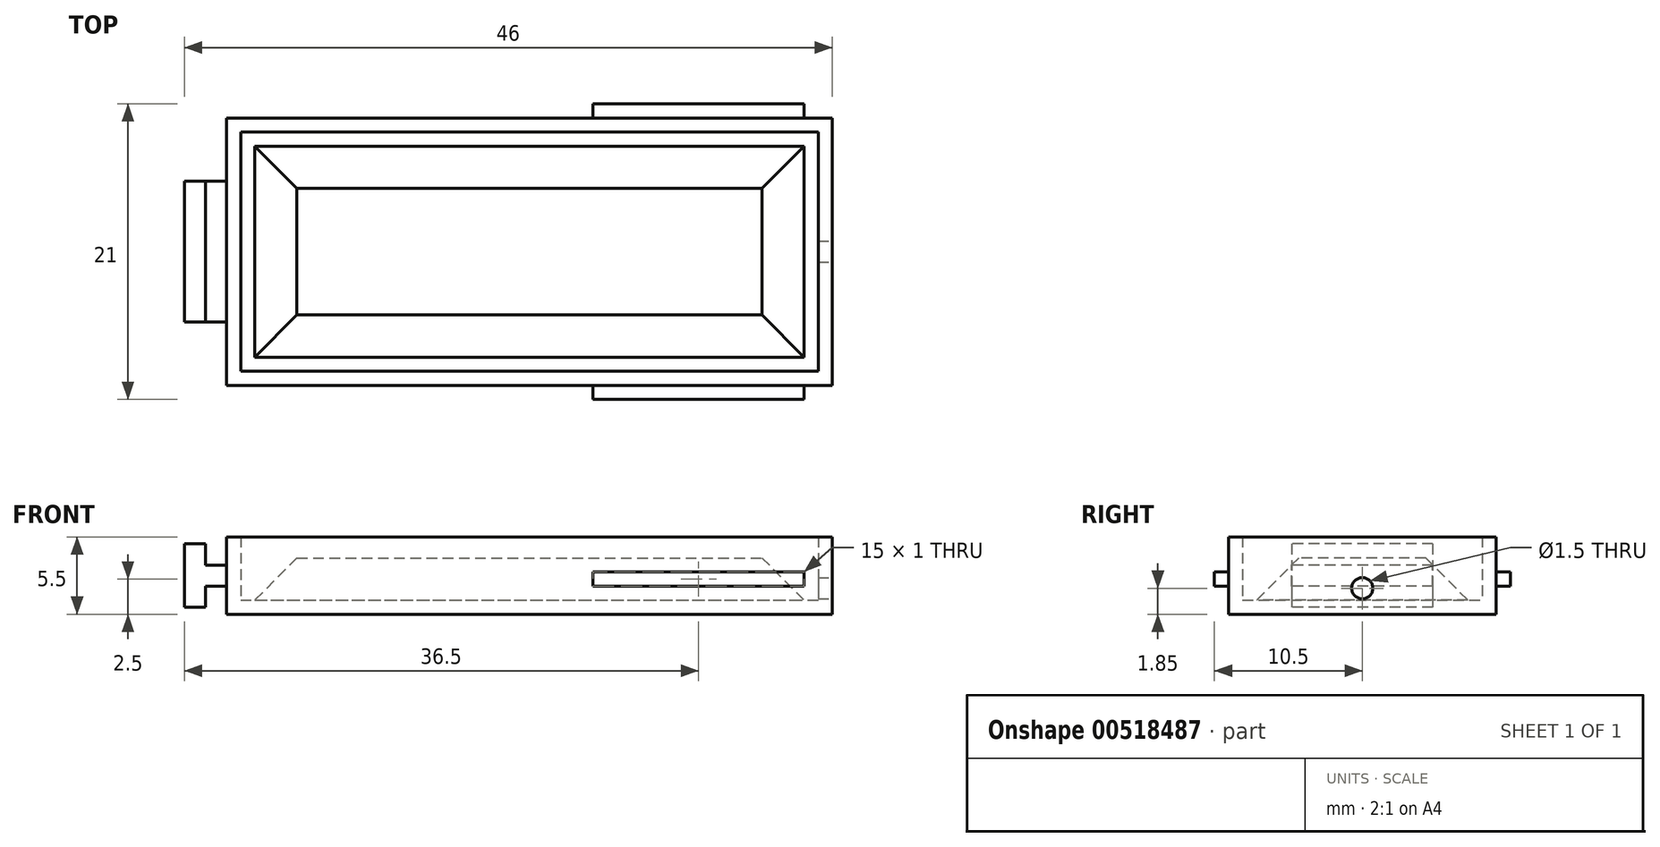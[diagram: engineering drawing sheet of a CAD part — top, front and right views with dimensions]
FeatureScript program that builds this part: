
annotation { "Feature Type Name" : "Feature", "Feature Type Description" : "" }
export const myFeature = defineFeature(function(context is Context, id is Id, definition is map)
    precondition{}
    {
        {
            var Q0;
            Q0=qCreatedBy(makeId("Top.planeOp"),FACE);
            var sketch = newSketch(context, id + "F0", { "sketchPlane" : qUnion([Q0])});
            skLineSegment(sketch, "E0.bottom", {"start": v(0, 9) * mm, "end": v(33, 9) * mm, "construction": true});
            skLineSegment(sketch, "E0.top", {"start": v(0, 0) * mm, "end": v(33, 0) * mm, "construction": true});
            skLineSegment(sketch, "E0.left", {"start": v(0, 9) * mm, "end": v(0, 0) * mm, "construction": true});
            skLineSegment(sketch, "E0.right", {"start": v(33, 9) * mm, "end": v(33, 0) * mm, "construction": true});
            skLineSegment(sketch, "E1.bottom", {"start": v(-3, 12) * mm, "end": v(36, 12) * mm});
            skLineSegment(sketch, "E1.top", {"start": v(-3, -3) * mm, "end": v(36, -3) * mm});
            skLineSegment(sketch, "E1.left", {"start": v(-3, 12) * mm, "end": v(-3, -3) * mm});
            skLineSegment(sketch, "E1.right", {"start": v(36, 12) * mm, "end": v(36, -3) * mm});
            skLineSegment(sketch, "E2", {"start": v(16.5, -23.39) * mm, "end": v(16.5, 35.98) * mm, "construction": true});
            skPoint(sketch, "E2.startSnap0", {"position": v(16.5, 12) * mm});
            skPoint(sketch, "E2.endSnap0", {"position": v(16.5, 12) * mm});
            skPoint(sketch, "E3", {"position": v(16.5, 0) * mm});
            skLineSegment(sketch, "E4", {"start": v(-3, 4.5) * mm, "end": v(36, 4.5) * mm, "construction": true});
            skPoint(sketch, "E4.startSnap0", {"position": v(0, 4.5) * mm});
            skPoint(sketch, "E4.startSnap1", {"position": v(-3, 4.5) * mm});
            skSolve(sketch);
        }
        {
            var Q0;
            Q0=qCreatedBy(makeId("Top.planeOp"),FACE);
            cPlane(context, id + "F1", {"entities" : qUnion([Q0]), "cplaneType" : CPlaneType.OFFSET, "offset" : 3 * mm, "width" : 150 * mm, "height" : 150 * mm});
        }
        {
            var Q0;
            Q0=qCreatedBy(id+"F1.planeOp",FACE);
            var sketch = newSketch(context, id + "F2", { "sketchPlane" : qUnion([Q0])});
            skLineSegment(sketch, "E5.0", {"start": v(0, 9) * mm, "end": v(33, 9) * mm});
            skLineSegment(sketch, "E5.1", {"start": v(0, 9) * mm, "end": v(0, 0) * mm});
            skLineSegment(sketch, "E5.2", {"start": v(0, 0) * mm, "end": v(33, 0) * mm});
            skLineSegment(sketch, "E5.3", {"start": v(33, 9) * mm, "end": v(33, 0) * mm});
            skLineSegment(sketch, "E6", {"start": v(0, 4.5) * mm, "end": v(33, 4.5) * mm, "construction": true});
            skSolve(sketch);
        }
        {
            var Q0;
            Q0=makeQuery(id+"F2.imprint","IMPRINT",FACE,{"disambiguationData":[TD([[makeQuery(id+"F2.imprint","IMPRINT",EDGE,{"derivedFrom":sQuery(id+"F2.wireOp",EDGE,"E5.0")}),-1.0]])]});
            var Q1;
            Q1=makeQuery(id+"F0.imprint","IMPRINT",FACE,{"disambiguationData":[TD([[makeQuery(id+"F0.imprint","IMPRINT",EDGE,{"derivedFrom":sQuery(id+"F0.wireOp",EDGE,"E1.bottom")}),-1.0]])]});
            loft(context, id + "F3", {"sheetProfilesArray" : [{ "sheetProfileEntities" : qUnion([Q0]) }, { "sheetProfileEntities" : qUnion([Q1]) }]});
        }
        {
            var Q0;
            Q0=qCreatedBy(id+"F1.planeOp",FACE);
            var sketch = newSketch(context, id + "F4", { "sketchPlane" : qUnion([Q0])});
            skLineSegment(sketch, "E7.0", {"start": v(0, 9) * mm, "end": v(33, 9) * mm, "construction": true});
            skLineSegment(sketch, "E7.1", {"start": v(0, 9) * mm, "end": v(0, 0) * mm, "construction": true});
            skLineSegment(sketch, "E7.2", {"start": v(0, 0) * mm, "end": v(33, 0) * mm, "construction": true});
            skLineSegment(sketch, "E7.3", {"start": v(33, 9) * mm, "end": v(33, 0) * mm, "construction": true});
            skLineSegment(sketch, "E8.bottom", {"start": v(25, 8) * mm, "end": v(32, 8) * mm});
            skLineSegment(sketch, "E8.top", {"start": v(25, 1) * mm, "end": v(32, 1) * mm});
            skLineSegment(sketch, "E8.left", {"start": v(25, 8) * mm, "end": v(25, 1) * mm});
            skLineSegment(sketch, "E8.right", {"start": v(32, 8) * mm, "end": v(32, 1) * mm});
            skLineSegment(sketch, "E9.1.0.0", {"start": v(17, 8) * mm, "end": v(24, 8) * mm});
            skLineSegment(sketch, "E9.1.0.1", {"start": v(17, 8) * mm, "end": v(17, 1) * mm});
            skLineSegment(sketch, "E9.1.0.2", {"start": v(17, 1) * mm, "end": v(24, 1) * mm});
            skLineSegment(sketch, "E9.1.0.3", {"start": v(24, 8) * mm, "end": v(24, 1) * mm});
            skLineSegment(sketch, "E9.2.0.0", {"start": v(9, 8) * mm, "end": v(16, 8) * mm});
            skLineSegment(sketch, "E9.2.0.1", {"start": v(9, 8) * mm, "end": v(9, 1) * mm});
            skLineSegment(sketch, "E9.2.0.2", {"start": v(9, 1) * mm, "end": v(16, 1) * mm});
            skLineSegment(sketch, "E9.2.0.3", {"start": v(16, 8) * mm, "end": v(16, 1) * mm});
            skLineSegment(sketch, "E9.3.0.0", {"start": v(1, 8) * mm, "end": v(8, 8) * mm});
            skLineSegment(sketch, "E9.3.0.1", {"start": v(1, 8) * mm, "end": v(1, 1) * mm});
            skLineSegment(sketch, "E9.3.0.2", {"start": v(1, 1) * mm, "end": v(8, 1) * mm});
            skLineSegment(sketch, "E9.3.0.3", {"start": v(8, 8) * mm, "end": v(8, 1) * mm});
            skLineSegment(sketch, "E9.direction1", {"start": v(25, 8) * mm, "end": v(17, 8) * mm, "construction": true});
            skSolve(sketch);
        }
        {
            var Q0;
            Q0=makeQuery(id+"F4.imprint","IMPRINT",FACE,{"disambiguationData":[TD([[makeQuery(id+"F4.imprint","IMPRINT",EDGE,{"derivedFrom":sQuery(id+"F4.wireOp",EDGE,"E8.bottom")}),-1.0]])]});
            var Q1;
            Q1=makeQuery(id+"F4.imprint","IMPRINT",FACE,{"disambiguationData":[TD([[makeQuery(id+"F4.imprint","IMPRINT",EDGE,{"derivedFrom":sQuery(id+"F4.wireOp",EDGE,"E9.1.0.0")}),-1.0]])]});
            var Q2;
            Q2=makeQuery(id+"F4.imprint","IMPRINT",FACE,{"disambiguationData":[TD([[makeQuery(id+"F4.imprint","IMPRINT",EDGE,{"derivedFrom":sQuery(id+"F4.wireOp",EDGE,"E9.2.0.0")}),-1.0]])]});
            var Q3;
            Q3=makeQuery(id+"F4.imprint","IMPRINT",FACE,{"disambiguationData":[TD([[makeQuery(id+"F4.imprint","IMPRINT",EDGE,{"derivedFrom":sQuery(id+"F4.wireOp",EDGE,"E9.3.0.0")}),-1.0]])]});
            extrude(context, id + "F5", {"entities" : qUnion([Q0, Q1, Q2, Q3]), "operationType" : NewBodyOperationType.REMOVE, "oppositeDirection" : true, "depth" : .5 * mm, "offsetDistance" : 25 * mm});
        }
        {
            var Q0;
            Q0=makeQuery(id+"F4.imprint","IMPRINT",FACE,{"disambiguationData":[TD([[makeQuery(id+"F4.imprint","IMPRINT",EDGE,{"derivedFrom":sQuery(id+"F4.wireOp",EDGE,"E9.3.0.0")}),-1.0]])]});
            var Q1;
            Q1=makeQuery(id+"F4.imprint","IMPRINT",FACE,{"disambiguationData":[TD([[makeQuery(id+"F4.imprint","IMPRINT",EDGE,{"derivedFrom":sQuery(id+"F4.wireOp",EDGE,"E9.2.0.0")}),-1.0]])]});
            var Q2;
            Q2=makeQuery(id+"F4.imprint","IMPRINT",FACE,{"disambiguationData":[TD([[makeQuery(id+"F4.imprint","IMPRINT",EDGE,{"derivedFrom":sQuery(id+"F4.wireOp",EDGE,"E9.1.0.0")}),-1.0]])]});
            var Q3;
            Q3=makeQuery(id+"F4.imprint","IMPRINT",FACE,{"disambiguationData":[TD([[makeQuery(id+"F4.imprint","IMPRINT",EDGE,{"derivedFrom":sQuery(id+"F4.wireOp",EDGE,"E8.bottom")}),-1.0]])]});
            extrude(context, id + "F6", {"entities" : qUnion([Q0, Q1, Q2, Q3]), "oppositeDirection" : true, "depth" : .5 * mm, "offsetDistance" : 25 * mm});
        }
        {
            var Q0;
            Q0=makeQuery(id+"F3.opLoft","CAP_FACE",FACE,{"disambiguationData":[OSD([makeQuery(id+"F0.imprint","IMPRINT",FACE,{"disambiguationData":[TD([[makeQuery(id+"F0.imprint","IMPRINT",EDGE,{"derivedFrom":sQuery(id+"F0.wireOp",EDGE,"E1.bottom")}),-1.0]])]})])],"isStart":true});
            var sketch = newSketch(context, id + "F7", { "sketchPlane" : qUnion([Q0])});
            skLineSegment(sketch, "E10", {"start": v(50.67, -4.5) * mm, "end": v(-14.18, -4.5) * mm, "construction": true});
            skPoint(sketch, "E10.startSnap0", {"position": v(36, -4.5) * mm});
            skPoint(sketch, "E10.endSnap0", {"position": v(-3, -4.5) * mm});
            skLineSegment(sketch, "E11.bottom", {"start": v(-4, 4) * mm, "end": v(37, 4) * mm});
            skLineSegment(sketch, "E11.top", {"start": v(-4, -13) * mm, "end": v(37, -13) * mm});
            skLineSegment(sketch, "E11.left", {"start": v(-4, 4) * mm, "end": v(-4, -13) * mm});
            skLineSegment(sketch, "E11.right", {"start": v(37, 4) * mm, "end": v(37, -13) * mm});
            skLineSegment(sketch, "E12.bottom", {"start": v(-5, 5) * mm, "end": v(38, 5) * mm});
            skLineSegment(sketch, "E12.top", {"start": v(-5, -14) * mm, "end": v(38, -14) * mm});
            skLineSegment(sketch, "E12.left", {"start": v(-5, 5) * mm, "end": v(-5, -14) * mm});
            skLineSegment(sketch, "E12.right", {"start": v(38, 5) * mm, "end": v(38, -14) * mm});
            skPoint(sketch, "E13", {"position": v(-4, -4.5) * mm});
            skPoint(sketch, "E14", {"position": v(-5, -4.5) * mm});
            skPoint(sketch, "E15", {"position": v(37, -4.5) * mm});
            skPoint(sketch, "E16", {"position": v(38, -4.5) * mm});
            skLineSegment(sketch, "E17", {"start": v(16.5, 6.06) * mm, "end": v(16.5, -15.03) * mm, "construction": true});
            skPoint(sketch, "E17.startSnap0", {"position": v(16.5, 3) * mm});
            skPoint(sketch, "E17.endSnap0", {"position": v(16.5, -12) * mm});
            skPoint(sketch, "E18", {"position": v(16.5, 4) * mm});
            skPoint(sketch, "E19", {"position": v(16.5, 5) * mm});
            skSolve(sketch);
        }
        {
            var Q0;
            {var subQ0=sQuery(id+"F0.wireOp",EDGE,"E1.right");var subQ1=sQuery(id+"F0.wireOp",EDGE,"E1.left");var subQ2=sQuery(id+"F0.wireOp",EDGE,"E1.bottom");Q0=makeQuery(id+"F7.imprint","IMPRINT",FACE,{"disambiguationData":[TD([[makeQuery(id+"F7.imprint","IMPRINT",EDGE,{"derivedFrom":makeQuery(id+"F3.opLoft","MID_CAP_EDGE",EDGE,{"disambiguationData":[OSD([subQ2,subQ1,subQ0])],"capPos":1.0})}),1.0]])]});}
            var Q1;
            Q1=makeQuery(id+"F7.imprint","IMPRINT",FACE,{"disambiguationData":[TD([[makeQuery(id+"F7.imprint","IMPRINT",EDGE,{"derivedFrom":sQuery(id+"F7.wireOp",EDGE,"E11.bottom")}),-1.0]])]});
            var Q2;
            Q2=makeQuery(id+"F7.imprint","IMPRINT",FACE,{"disambiguationData":[TD([[makeQuery(id+"F7.imprint","IMPRINT",EDGE,{"derivedFrom":sQuery(id+"F7.wireOp",EDGE,"E11.bottom")}),1.0]])]});
            extrude(context, id + "F8", {"entities" : qUnion([Q0, Q1, Q2]), "operationType" : NewBodyOperationType.ADD, "depth" : 1 * mm, "offsetDistance" : 25 * mm});
        }
        {
            var Q0;
            Q0=makeQuery(id+"F7.imprint","IMPRINT",FACE,{"disambiguationData":[TD([[makeQuery(id+"F7.imprint","IMPRINT",EDGE,{"derivedFrom":sQuery(id+"F7.wireOp",EDGE,"E11.bottom")}),1.0]])]});
            extrude(context, id + "F9", {"entities" : qUnion([Q0]), "operationType" : NewBodyOperationType.ADD, "oppositeDirection" : true, "depth" : 4.5 * mm, "offsetDistance" : 25 * mm});
        }
        {
            var Q0;
            {var subQ0=sQuery(id+"F7.wireOp",EDGE,"E12.right");Q0=makeQuery(id+"F9.boolean.opBoolean","MERGE",FACE,{"derivedFrom":[makeQuery(id+"F8.opExtrude","SWEPT_FACE",FACE,{"disambiguationData":[OSD([subQ0])]}),makeQuery(id+"F9.opExtrude","SWEPT_FACE",FACE,{"disambiguationData":[OSD([subQ0])]})]});}
            var sketch = newSketch(context, id + "F10", { "sketchPlane" : qUnion([Q0])});
            skCircle(sketch, "E20", {"center": v(4.5, 0.85) * mm, "radius": 0.75 * mm});
            skLineSegment(sketch, "E21", {"start": v(4.5, -0.43) * mm, "end": v(4.5, 2.94) * mm, "construction": true});
            skPoint(sketch, "E21.startSnap0", {"position": v(4.5, 0) * mm});
            skSolve(sketch);
        }
        {
            var Q0;
            Q0=makeQuery(id+"F10.imprint","IMPRINT",FACE,{"disambiguationData":[TD([[makeQuery(id+"F10.imprint","IMPRINT",EDGE,{"derivedFrom":sQuery(id+"F10.wireOp",EDGE,"E20")}),1.0]])]});
            var Q1;
            Q1=makeQuery(id+"F3.opLoft","SWEPT_BODY",BODY,{"disambiguationData":[OSD([makeQuery(id+"F0.imprint","IMPRINT",FACE,{"disambiguationData":[TD([[makeQuery(id+"F0.imprint","IMPRINT",EDGE,{"derivedFrom":sQuery(id+"F0.wireOp",EDGE,"E1.bottom")}),-1.0]])]}),makeQuery(id+"F2.imprint","IMPRINT",FACE,{"disambiguationData":[TD([[makeQuery(id+"F2.imprint","IMPRINT",EDGE,{"derivedFrom":sQuery(id+"F2.wireOp",EDGE,"E5.0")}),-1.0]])]})])]});
            extrude(context, id + "F11", {"entities" : qUnion([Q0]), "operationType" : NewBodyOperationType.REMOVE, "endBound" : BoundingType.UP_TO_BODY, "oppositeDirection" : true, "depth" : 25 * mm, "endBoundEntityBody" : qUnion([Q1]), "offsetDistance" : 25 * mm});
        }
        {
            var Q0;
            {var subQ0=sQuery(id+"F7.wireOp",EDGE,"E12.bottom");Q0=makeQuery(id+"F9.boolean.opBoolean","MERGE",FACE,{"derivedFrom":[makeQuery(id+"F8.opExtrude","SWEPT_FACE",FACE,{"disambiguationData":[OSD([subQ0])]}),makeQuery(id+"F9.opExtrude","SWEPT_FACE",FACE,{"disambiguationData":[OSD([subQ0])]})]});}
            var sketch = newSketch(context, id + "F12", { "sketchPlane" : qUnion([Q0])});
            skLineSegment(sketch, "E22.bottom", {"start": v(21, 2) * mm, "end": v(36, 2) * mm});
            skLineSegment(sketch, "E22.top", {"start": v(21, 1) * mm, "end": v(36, 1) * mm});
            skLineSegment(sketch, "E22.left", {"start": v(21, 2) * mm, "end": v(21, 1) * mm});
            skLineSegment(sketch, "E22.right", {"start": v(36, 2) * mm, "end": v(36, 1) * mm});
            skSolve(sketch);
        }
        {
            var Q0;
            Q0=makeQuery(id+"F12.imprint","IMPRINT",FACE,{"disambiguationData":[TD([[makeQuery(id+"F12.imprint","IMPRINT",EDGE,{"derivedFrom":sQuery(id+"F12.wireOp",EDGE,"E22.bottom")}),-1.0]])]});
            extrude(context, id + "F13", {"entities" : qUnion([Q0]), "operationType" : NewBodyOperationType.ADD, "depth" : 1 * mm, "offsetDistance" : 25 * mm});
        }
        {
            var Q0;
            Q0=makeQuery(id+"F9.opExtrude","CAP_EDGE",EDGE,{"disambiguationData":[OSD([sQuery(id+"F7.wireOp",EDGE,"E12.right")])],"isStart":false});
            cPoint(context, id + "F14", {"entities" : qUnion([Q0]), "parameter" : 0.5});
        }
        {
            var Q0;
            Q0=sQuery(id+"F7.wireOp",EDGE,"E10");
            var Q1;
            Q1 = qCreatedBy(id + "F14" ,VERTEX);
            cPlane(context, id + "F15", {"entities" : qUnion([Q0, Q1]), "cplaneType" : CPlaneType.LINE_ANGLE, "offset" : 25 * mm, "angle" : 0 * degree, "width" : 150 * mm, "height" : 150 * mm});
        }
        {
            var Q0;
            Q0=makeQuery(id+"F3.opLoft","SWEPT_BODY",BODY,{"disambiguationData":[OSD([makeQuery(id+"F0.imprint","IMPRINT",FACE,{"disambiguationData":[TD([[makeQuery(id+"F0.imprint","IMPRINT",EDGE,{"derivedFrom":sQuery(id+"F0.wireOp",EDGE,"E1.bottom")}),-1.0]])]}),makeQuery(id+"F2.imprint","IMPRINT",FACE,{"disambiguationData":[TD([[makeQuery(id+"F2.imprint","IMPRINT",EDGE,{"derivedFrom":sQuery(id+"F2.wireOp",EDGE,"E5.0")}),-1.0]])]})])]});
            var Q1;
            Q1=qCreatedBy(id+"F15.planeOp",FACE);
            mirror(context, id + "F16", {"operationType" : NewBodyOperationType.ADD, "entities" : qUnion([Q0]), "mirrorPlane" : qUnion([Q1])});
        }
        {
            var Q0;
            Q0=qCreatedBy(id+"F15.planeOp",FACE);
            var sketch = newSketch(context, id + "F17", { "sketchPlane" : qUnion([Q0])});
            skLineSegment(sketch, "E23.0", {"start": v(5, -1) * mm, "end": v(5, 4.5) * mm});
            skLineSegment(sketch, "E24.bottom", {"start": v(8, 4) * mm, "end": v(6.5, 4) * mm});
            skLineSegment(sketch, "E24.top", {"start": v(8, -0.5) * mm, "end": v(6.5, -0.5) * mm});
            skLineSegment(sketch, "E24.left", {"start": v(8, 4) * mm, "end": v(8, -0.5) * mm});
            skLineSegment(sketch, "E24.right", {"start": v(6.5, 4) * mm, "end": v(6.5, -0.5) * mm});
            skLineSegment(sketch, "E25.bottom", {"start": v(6.5, 2.5) * mm, "end": v(5, 2.5) * mm});
            skLineSegment(sketch, "E25.top", {"start": v(6.5, 1) * mm, "end": v(5, 1) * mm});
            skLineSegment(sketch, "E25.left", {"start": v(6.5, 1.75) * mm, "end": v(6.5, 1) * mm});
            skLineSegment(sketch, "E25.right", {"start": v(5, 2.5) * mm, "end": v(5, 1) * mm});
            skLineSegment(sketch, "E26", {"start": v(8, 1.75) * mm, "end": v(5, 1.75) * mm, "construction": true});
            skPoint(sketch, "E27", {"position": v(6.5, 1.75) * mm});
            skSolve(sketch);
        }
        {
            var Q0;
            {var subQ1=sQuery(id+"F17.wireOp",EDGE,"E24.bottom");Q0=makeQuery(id+"F17.imprint","IMPRINT",FACE,{"disambiguationData":[TD([[makeQuery(id+"F17.imprint","IMPRINT",EDGE,{"derivedFrom":subQ1}),1.0]])]});}
            var Q1;
            {var subQ1=sQuery(id+"F17.wireOp",EDGE,"E25.bottom");Q1=makeQuery(id+"F17.imprint","IMPRINT",FACE,{"disambiguationData":[TD([[makeQuery(id+"F17.imprint","IMPRINT",EDGE,{"derivedFrom":subQ1}),1.0]])]});}
            extrude(context, id + "F18", {"entities" : qUnion([Q0, Q1]), "operationType" : NewBodyOperationType.ADD, "endBound" : BoundingType.SYMMETRIC, "depth" : 10 * mm, "offsetDistance" : 25 * mm});
        }
    });
